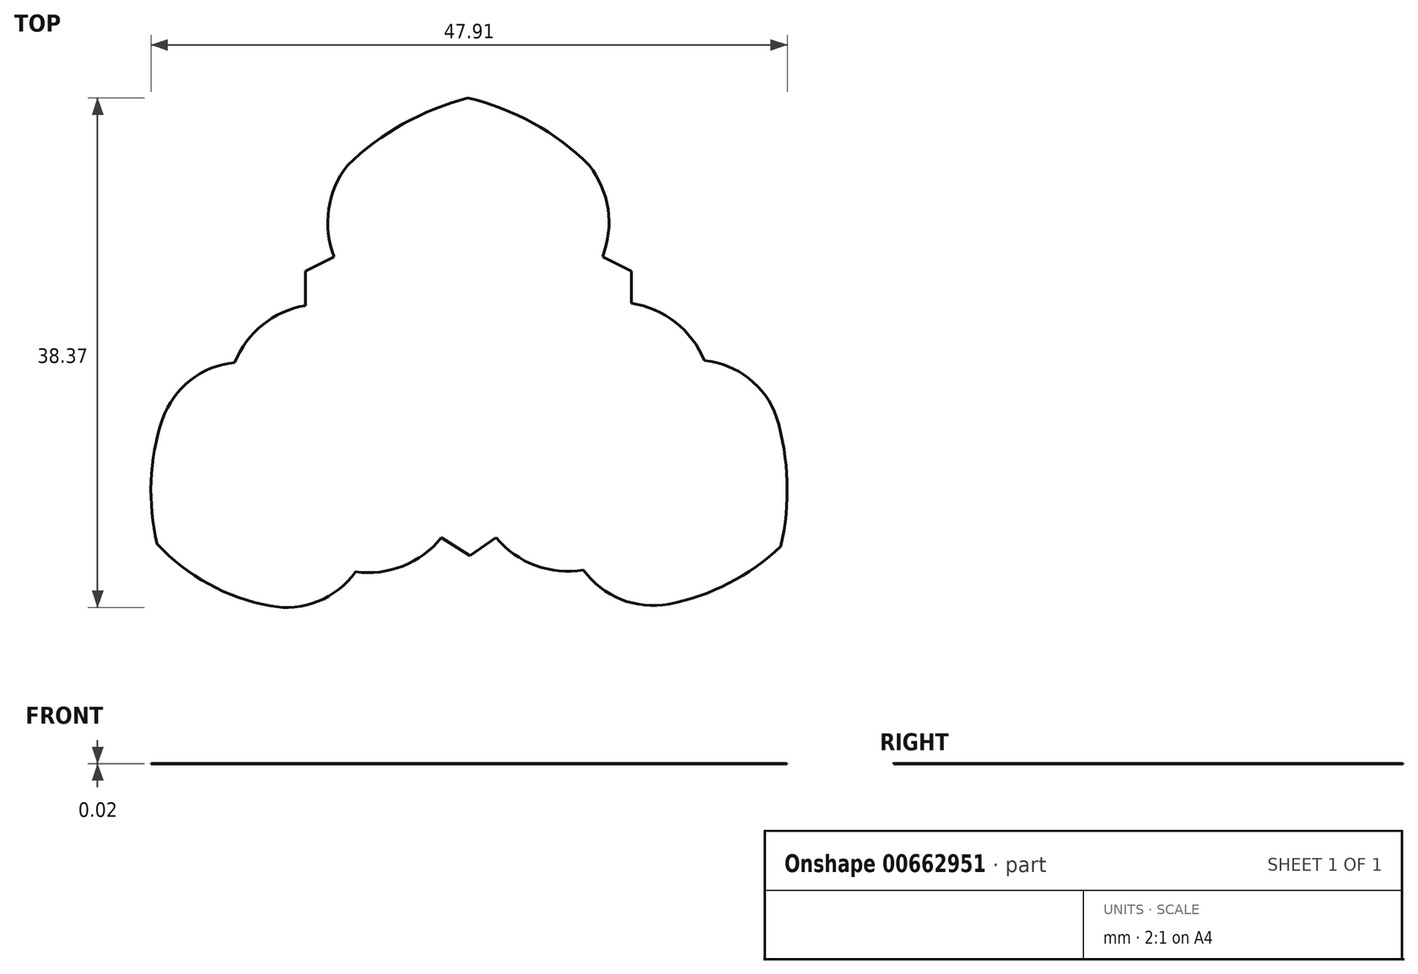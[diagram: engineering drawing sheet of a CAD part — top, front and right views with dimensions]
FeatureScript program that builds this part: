
annotation { "Feature Type Name" : "Feature", "Feature Type Description" : "" }
export const myFeature = defineFeature(function(context is Context, id is Id, definition is map)
    precondition{}
    {
        {
            var Q0;
            Q0=qCreatedBy(makeId("Top.planeOp"),FACE);
            var sketch = newSketch(context, id + "F0", { "sketchPlane" : qUnion([Q0])});
            skPoint(sketch, "E0.center", {"position": v(0, 0) * mm});
            skArc(sketch, "E1", {"start": v(-9.2, 15.13) * mm, "mid": v(-10.62, 11.82) * mm, "end": v(-10.2, 8.25) * mm});
            skLineSegment(sketch, "E2", {"start": v(-10.2, 8.25) * mm, "end": v(-12.37, 7.15) * mm});
            skLineSegment(sketch, "E3", {"start": v(-12.37, 7.15) * mm, "end": v(-12.37, 4.64) * mm});
            skLineSegment(sketch, "E4.MirrorCS", {"start": v(12.16, 7.15) * mm, "end": v(12.16, 4.64) * mm});
            skLineSegment(sketch, "E5.MirrorCS", {"start": v(10, 8.25) * mm, "end": v(12.16, 7.15) * mm});
            skArc(sketch, "E6.MirrorCS", {"start": v(9, 15.13) * mm, "mid": v(10.4, 11.82) * mm, "end": v(10, 8.25) * mm});
            skArc(sketch, "E7", {"start": v(23.1, -3.85) * mm, "mid": v(21, -0.92) * mm, "end": v(17.66, 0.43) * mm});
            skArc(sketch, "E8", {"start": v(17.66, 0.43) * mm, "mid": v(15.48, 3.32) * mm, "end": v(12.16, 4.74) * mm});
            skArc(sketch, "E9.MirrorCS", {"start": v(8.56, -15.34) * mm, "mid": v(4.94, -15) * mm, "end": v(1.97, -12.9) * mm});
            skArc(sketch, "E10.MirrorCS", {"start": v(14.98, -17.91) * mm, "mid": v(11.4, -17.56) * mm, "end": v(8.56, -15.34) * mm});
            skLineSegment(sketch, "E11", {"start": v(1.97, -12.9) * mm, "end": v(0, -14.26) * mm});
            skLineSegment(sketch, "E12", {"start": v(0, -14.26) * mm, "end": v(-2.14, -12.9) * mm});
            skArc(sketch, "E13", {"start": v(-15.02, -18.05) * mm, "mid": v(-11.43, -17.7) * mm, "end": v(-8.6, -15.48) * mm});
            skArc(sketch, "E14", {"start": v(-8.6, -15.48) * mm, "mid": v(-5.03, -15.05) * mm, "end": v(-2.14, -12.9) * mm});
            skArc(sketch, "E15.MirrorCS", {"start": v(-17.7, 0.28) * mm, "mid": v(-15.6, 3.12) * mm, "end": v(-12.37, 4.57) * mm});
            skArc(sketch, "E16.MirrorCS", {"start": v(-23.14, -4) * mm, "mid": v(-21.05, -1.06) * mm, "end": v(-17.7, 0.28) * mm});
            skLineSegment(sketch, "E17", {"start": v(-12.37, 4.64) * mm, "end": v(-12.37, 4.57) * mm});
            skArc(sketch, "E18", {"start": v(23.42, -13.56) * mm, "mid": v(23.89, -8.68) * mm, "end": v(23.1, -3.85) * mm});
            skArc(sketch, "E19", {"start": v(14.98, -17.91) * mm, "mid": v(19.52, -16.35) * mm, "end": v(23.42, -13.56) * mm});
            skArc(sketch, "E20", {"start": v(-23.14, -4) * mm, "mid": v(-24, -8.66) * mm, "end": v(-23.53, -13.39) * mm});
            skArc(sketch, "E21", {"start": v(-23.53, -13.39) * mm, "mid": v(-19.66, -16.41) * mm, "end": v(-15.02, -18.05) * mm});
            skArc(sketch, "E22", {"start": v(-0.14, 20.2) * mm, "mid": v(-5, 18.26) * mm, "end": v(-9.2, 15.13) * mm});
            skArc(sketch, "E23", {"start": v(9, 15.13) * mm, "mid": v(4.78, 18.3) * mm, "end": v(-0.14, 20.2) * mm});
            skSolve(sketch);
        }
        {
            var Q0;
            Q0=makeQuery(id+"F0.imprint","IMPRINT",FACE,{"disambiguationData":[TD([[makeQuery(id+"F0.imprint","IMPRINT",EDGE,{"derivedFrom":sQuery(id+"F0.wireOp",EDGE,"E1")}),1.0]])]});
            extrude(context, id + "F1", {"entities" : qUnion([Q0]), "depth" : 7 / 406.4 * mm, "offsetDistance" : 25.4 * mm});
        }
    });
